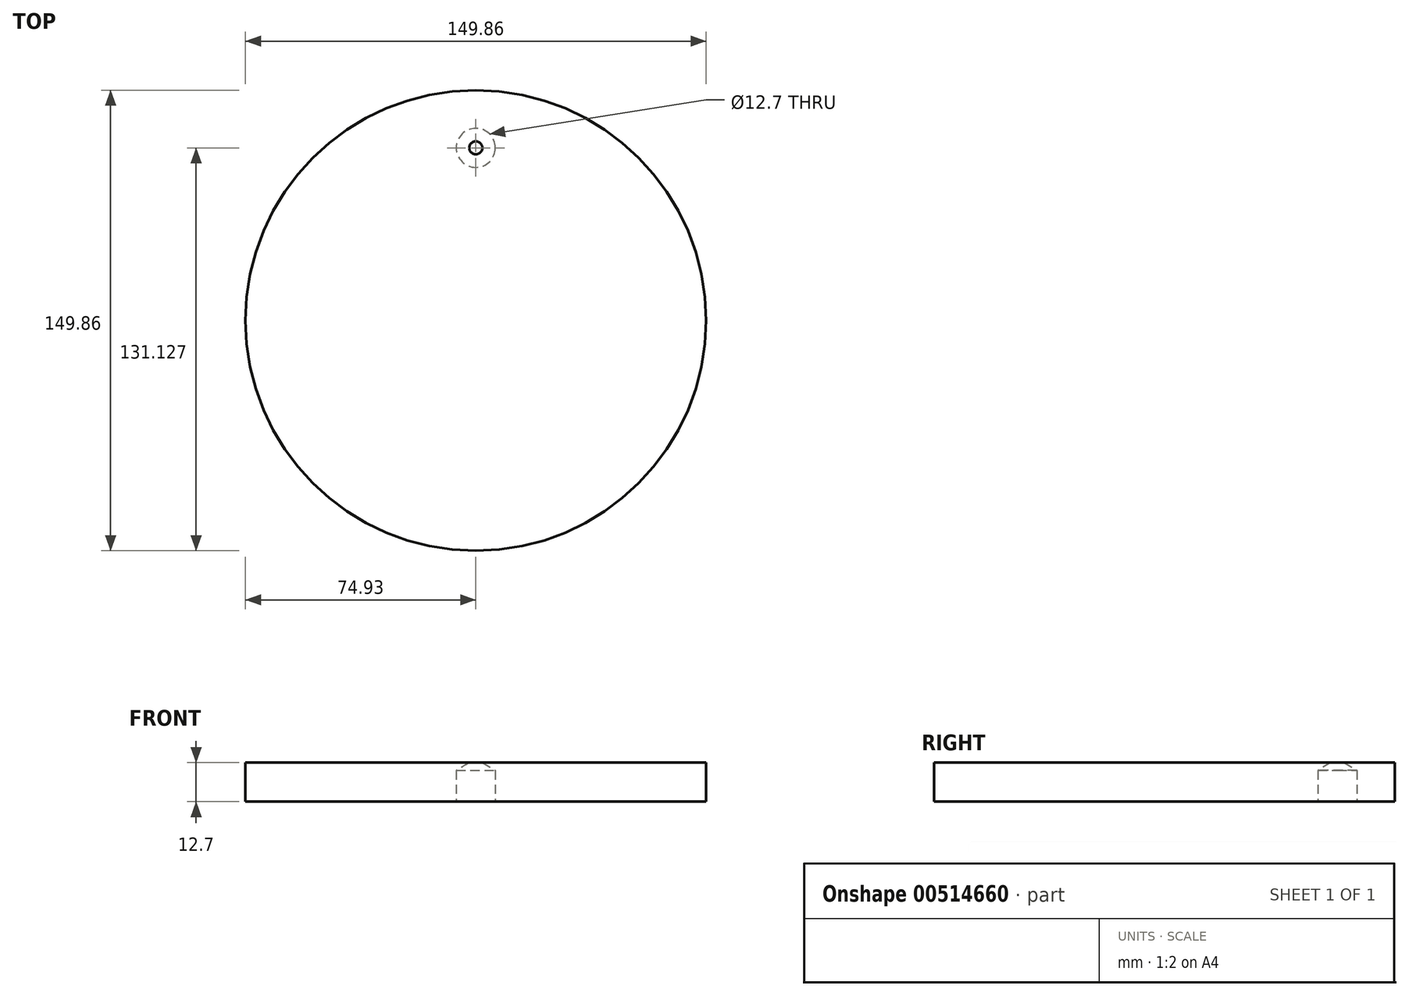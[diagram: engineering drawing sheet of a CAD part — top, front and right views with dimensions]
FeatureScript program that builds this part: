
annotation { "Feature Type Name" : "Feature", "Feature Type Description" : "" }
export const myFeature = defineFeature(function(context is Context, id is Id, definition is map)
    precondition{}
    {
        {
            var Q0;
            Q0=qCreatedBy(makeId("Top.planeOp"),FACE);
            var sketch = newSketch(context, id + "F0", { "sketchPlane" : qUnion([Q0])});
            skCircle(sketch, "E0", {"center": v(0, 0) * mm, "radius": 74.93 * mm});
            skSolve(sketch);
        }
        {
            var Q0;
            Q0=makeQuery(id+"F0.imprint","IMPRINT",FACE,{"disambiguationData":[TD([[makeQuery(id+"F0.imprint","IMPRINT",EDGE,{"derivedFrom":sQuery(id+"F0.wireOp",EDGE,"E0")}),1.0]])]});
            extrude(context, id + "F1", {"entities" : qUnion([Q0]), "endBound" : BoundingType.SYMMETRIC, "depth" : 12.7 * mm});
        }
        {
            var Q0;
            Q0=makeQuery(id+"F1.opExtrude","CAP_FACE",FACE,{"disambiguationData":[OSD([sQuery(id+"F0.wireOp",EDGE,"E0")])],"isStart":true});
            var sketch = newSketch(context, id + "F2", { "sketchPlane" : qUnion([Q0])});
            skCircle(sketch, "E1", {"center": v(0, -56.2) * mm, "radius": 6.35 * mm});
            skSolve(sketch);
        }
        {
            var Q0;
            Q0=sQuery(id+"F2.wireOp",VERTEX,"E1.center");
            var Q1;
            Q1=makeQuery(id+"F1.opExtrude","SWEPT_BODY",BODY,{"disambiguationData":[OSD([sQuery(id+"F0.wireOp",EDGE,"E0")])]});
            hole(context, id + "F3", {"style" : HoleStyle.SIMPLE, "endStyle" : HoleEndStyle.BLIND, "holeDiameter" : 12.7 * mm, "majorDiameter" : 6.35 * mm, "holeDepth" : 10.16 * mm, "isTappedThrough" : true, "tappedDepth" : 12.7 * mm, "tapClearance" : 3, "locations" : qUnion([Q0]), "scope" : qUnion([Q1])});
        }
    });
